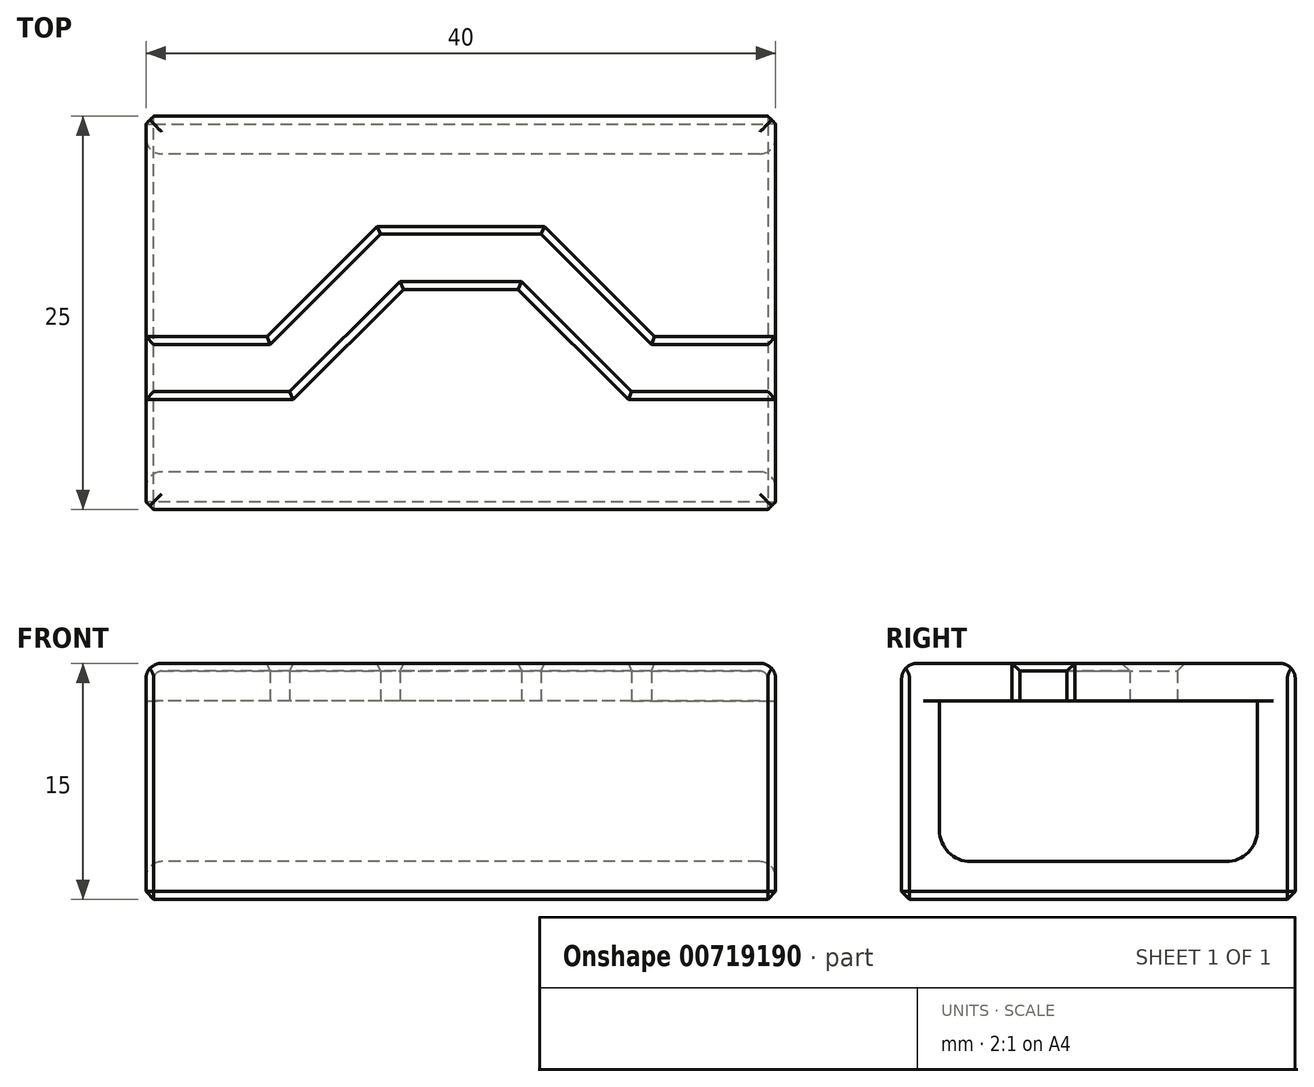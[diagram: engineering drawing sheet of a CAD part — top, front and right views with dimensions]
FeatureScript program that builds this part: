
annotation { "Feature Type Name" : "Feature", "Feature Type Description" : "" }
export const myFeature = defineFeature(function(context is Context, id is Id, definition is map)
    precondition{}
    {
        {
            var Q0;
            Q0=qCreatedBy(makeId("Right.planeOp"),FACE);
            var sketch = newSketch(context, id + "F0", { "sketchPlane" : qUnion([Q0])});
            skLineSegment(sketch, "E0.bottom", {"start": v(-8.1, -5.1) * mm, "end": v(8.1, -5.1) * mm});
            skLineSegment(sketch, "E0.top", {"start": v(-10.1, 5.1) * mm, "end": v(10.1, 5.1) * mm});
            skLineSegment(sketch, "E0.left", {"start": v(-10.1, -3.1) * mm, "end": v(-10.1, 5.1) * mm});
            skLineSegment(sketch, "E0.right", {"start": v(10.1, -3.1) * mm, "end": v(10.1, 5.1) * mm});
            skPoint(sketch, "E0.middle", {"position": v(0, 0) * mm});
            skLineSegment(sketch, "E1.bottom", {"start": v(-12.5, -7.5) * mm, "end": v(12.5, -7.5) * mm});
            skLineSegment(sketch, "E1.top", {"start": v(-12.5, 7.5) * mm, "end": v(12.5, 7.5) * mm});
            skLineSegment(sketch, "E1.left", {"start": v(-12.5, -7.5) * mm, "end": v(-12.5, 7.5) * mm});
            skLineSegment(sketch, "E1.right", {"start": v(12.5, -7.5) * mm, "end": v(12.5, 7.5) * mm});
            skPoint(sketch, "E2.visualSharp", {"position": v(-10.1, -5.1) * mm});
            skArc(sketch, "E2.filletArc", {"start": v(-10.1, -3.1) * mm, "mid": v(-9.51, -4.51) * mm, "end": v(-8.1, -5.1) * mm});
            skPoint(sketch, "E3.visualSharp", {"position": v(10.1, -5.1) * mm});
            skArc(sketch, "E3.filletArc", {"start": v(8.1, -5.1) * mm, "mid": v(9.51, -4.51) * mm, "end": v(10.1, -3.1) * mm});
            skSolve(sketch);
        }
        {
            var Q0;
            Q0 = qSketchRegion(id + "F0", true);
            extrude(context, id + "F1", {"entities" : qUnion([Q0]), "endBound" : BoundingType.SYMMETRIC, "depth" : 40 * mm, "offsetDistance" : 25 * mm});
        }
        {
            var Q0;
            Q0=qCreatedBy(makeId("Top.planeOp"),FACE);
            var sketch = newSketch(context, id + "F2", { "sketchPlane" : qUnion([Q0])});
            skLineSegment(sketch, "E4", {"start": v(5.1, 5) * mm, "end": v(12.1, -2) * mm});
            skLineSegment(sketch, "E5", {"start": v(-10.86, -5) * mm, "end": v(-3.86, 2) * mm});
            skLineSegment(sketch, "E6", {"start": v(3.86, 2) * mm, "end": v(10.86, -5) * mm});
            skLineSegment(sketch, "E7", {"start": v(-3.86, 2) * mm, "end": v(3.86, 2) * mm});
            skPoint(sketch, "E8.orphan", {"position": v(0, 5.86) * mm});
            skLineSegment(sketch, "E9", {"start": v(-5.1, 5) * mm, "end": v(5.1, 5) * mm});
            skPoint(sketch, "E10.orphan", {"position": v(0, 10.1) * mm});
            skLineSegment(sketch, "E11", {"start": v(-75, -2) * mm, "end": v(-12.1, -2) * mm});
            skLineSegment(sketch, "E12", {"start": v(75, -2) * mm, "end": v(12.1, -2) * mm});
            skLineSegment(sketch, "E13", {"start": v(75, -5) * mm, "end": v(10.86, -5) * mm});
            skLineSegment(sketch, "E14", {"start": v(-75, -5) * mm, "end": v(-10.86, -5) * mm});
            skLineSegment(sketch, "E15", {"start": v(-75, -2) * mm, "end": v(-75, -5) * mm});
            skLineSegment(sketch, "E16", {"start": v(75, -2) * mm, "end": v(75, -5) * mm});
            skLineSegment(sketch, "E17.trimOffspring", {"start": v(-12.1, -2) * mm, "end": v(-5.1, 5) * mm});
            skSolve(sketch);
        }
        {
            var Q0;
            Q0 = qSketchRegion(id + "F2", true);
            extrude(context, id + "F3", {"entities" : qUnion([Q0]), "operationType" : NewBodyOperationType.REMOVE, "endBound" : BoundingType.THROUGH_ALL, "depth" : 25 * mm, "offsetDistance" : 25 * mm});
        }
        {
            var Q0;
            Q0=makeQuery(id+"F1.opExtrude","CAP_EDGE",EDGE,{"disambiguationData":[OSD([sQuery(id+"F0.wireOp",EDGE,"E0.bottom")])],"isStart":false});
            var Q1;
            Q1=makeQuery(id+"F1.opExtrude","CAP_EDGE",EDGE,{"disambiguationData":[OSD([sQuery(id+"F0.wireOp",EDGE,"E0.bottom")])],"isStart":true});
            var Q2;
            Q2=makeQuery(id+"F1.opExtrude","SWEPT_EDGE",EDGE,{"disambiguationData":[OSD([sQuery(id+"F0.wireOp",EDGE,"E1.top"),sQuery(id+"F0.wireOp",EDGE,"E1.left")])]});
            var Q3;
            Q3=makeQuery(id+"F1.opExtrude","SWEPT_EDGE",EDGE,{"disambiguationData":[OSD([sQuery(id+"F0.wireOp",EDGE,"E1.top"),sQuery(id+"F0.wireOp",EDGE,"E1.right")])]});
            var Q4;
            {var subQ0=sQuery(id+"F0.wireOp",EDGE,"E1.right");var subQ1=sQuery(id+"F0.wireOp",EDGE,"E1.top");Q4=makeQuery(id+"F3.boolean.opBoolean","SPLIT",EDGE,{"disambiguationData":[TD([makeQuery(id+"F1.opExtrude","SWEPT_FACE",FACE,{"disambiguationData":[OSD([subQ0])]})])],"derivedFrom":makeQuery(id+"F1.opExtrude","CAP_EDGE",EDGE,{"disambiguationData":[OSD([subQ1])],"isStart":true})});}
            var Q5;
            {var subQ0=sQuery(id+"F0.wireOp",EDGE,"E1.left");var subQ1=sQuery(id+"F0.wireOp",EDGE,"E1.top");Q5=makeQuery(id+"F3.boolean.opBoolean","SPLIT",EDGE,{"disambiguationData":[TD([makeQuery(id+"F1.opExtrude","SWEPT_FACE",FACE,{"disambiguationData":[OSD([subQ0])]})])],"derivedFrom":makeQuery(id+"F1.opExtrude","CAP_EDGE",EDGE,{"disambiguationData":[OSD([subQ1])],"isStart":true})});}
            var Q6;
            {var subQ0=sQuery(id+"F0.wireOp",EDGE,"E1.right");var subQ1=sQuery(id+"F0.wireOp",EDGE,"E1.top");Q6=makeQuery(id+"F3.boolean.opBoolean","SPLIT",EDGE,{"disambiguationData":[TD([makeQuery(id+"F1.opExtrude","SWEPT_FACE",FACE,{"disambiguationData":[OSD([subQ0])]})])],"derivedFrom":makeQuery(id+"F1.opExtrude","CAP_EDGE",EDGE,{"disambiguationData":[OSD([subQ1])],"isStart":false})});}
            var Q7;
            {var subQ0=sQuery(id+"F0.wireOp",EDGE,"E1.left");var subQ1=sQuery(id+"F0.wireOp",EDGE,"E1.top");Q7=makeQuery(id+"F3.boolean.opBoolean","SPLIT",EDGE,{"disambiguationData":[TD([makeQuery(id+"F1.opExtrude","SWEPT_FACE",FACE,{"disambiguationData":[OSD([subQ0])]})])],"derivedFrom":makeQuery(id+"F1.opExtrude","CAP_EDGE",EDGE,{"disambiguationData":[OSD([subQ1])],"isStart":false})});}
            fillet(context, id + "F4", {"entities" : qUnion([Q0, Q1, Q2, Q3, Q4, Q5, Q6, Q7]), "radius" : 1 * mm, "tangentPropagation" : true, "allowEdgeOverflow" : false});
        }
        {
            var Q0;
            {var subQ2=sQuery(id+"F0.wireOp",EDGE,"E1.right");var subQ4=sQuery(id+"F0.wireOp",EDGE,"E1.top");Q0=makeQuery(id+"F3.boolean.opBoolean","SPLIT",FACE,{"disambiguationData":[TD([makeQuery(id+"F1.opExtrude","SWEPT_FACE",FACE,{"disambiguationData":[OSD([subQ2])]})])],"derivedFrom":makeQuery(id+"F1.opExtrude","SWEPT_FACE",FACE,{"disambiguationData":[OSD([subQ4])]})});}
            var Q1;
            {var subQ0=sQuery(id+"F0.wireOp",EDGE,"E1.left");var subQ4=sQuery(id+"F0.wireOp",EDGE,"E1.top");Q1=makeQuery(id+"F3.boolean.opBoolean","SPLIT",FACE,{"disambiguationData":[TD([makeQuery(id+"F1.opExtrude","SWEPT_FACE",FACE,{"disambiguationData":[OSD([subQ0])]})])],"derivedFrom":makeQuery(id+"F1.opExtrude","SWEPT_FACE",FACE,{"disambiguationData":[OSD([subQ4])]})});}
            var Q2;
            Q2=makeQuery(id+"F1.opExtrude","SWEPT_FACE",FACE,{"disambiguationData":[OSD([sQuery(id+"F0.wireOp",EDGE,"E1.left")])]});
            var Q3;
            Q3=makeQuery(id+"F1.opExtrude","SWEPT_FACE",FACE,{"disambiguationData":[OSD([sQuery(id+"F0.wireOp",EDGE,"E1.right")])]});
            var Q4;
            Q4=makeQuery(id+"F1.opExtrude","SWEPT_FACE",FACE,{"disambiguationData":[OSD([sQuery(id+"F0.wireOp",EDGE,"E1.bottom")])]});
            chamfer(context, id + "F5", {"entities" : qUnion([Q0, Q1, Q2, Q3, Q4]), "width" : .5 * mm, "tangentPropagation" : true});
        }
    });
